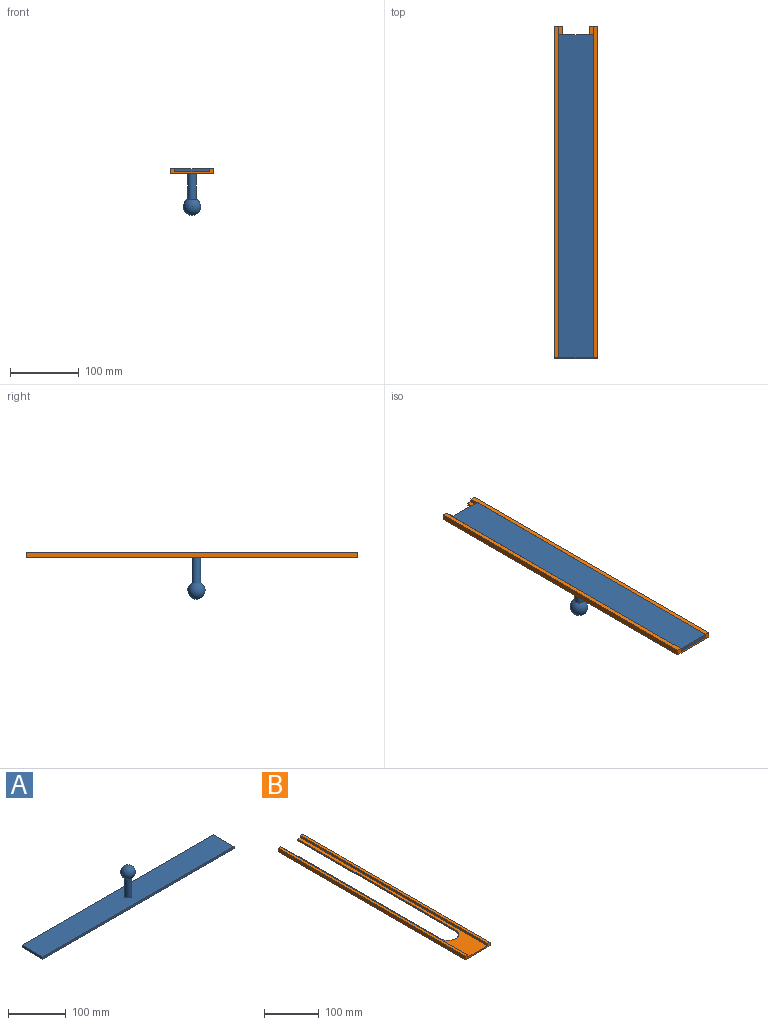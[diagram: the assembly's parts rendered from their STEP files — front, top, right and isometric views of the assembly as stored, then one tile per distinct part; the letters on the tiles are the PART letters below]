
ASSEMBLY  parts=2 mates=1
PART A: 8 faces, bbox 469.9x50.8x68.3 mm
  f0: cylinder r=6.35mm len=39.8mm, axis (0,0,-1), area 1588mm2, adj f5,f7
  f1: plane 50.8x4.76mm, normal (-1,0,0), area 241.9mm2, adj f2,f4,f5,f6
  f2: plane 469.9x4.76mm, normal (0,-1,0), area 2237.9mm2, adj f1,f3,f5,f6
  f3: plane 50.8x4.76mm, normal (1,0,0), area 241.9mm2, adj f2,f4,f5,f6
  f4: plane 469.9x4.76mm, normal (0,1,0), area 2237.9mm2, adj f1,f3,f5,f6
  f5: plane 469.9x50.8mm, normal (0,0,1), area 23744.2mm2, adj f0,f1,f2,f3,f4
  f6: plane 469.9x50.8mm, normal (0,0,-1), area 23870.9mm2, adj f1,f2,f3,f4
  f7: sphere r=12.7mm, area 1891.1mm2, adj f0
PART B: 14 faces, bbox 63.5x482.6x7.9 mm
  f0: plane 482.6x63.5mm, normal (0,0,-1), area 14591.2mm2, adj f2,f3,f8,f9,f10,f11,f12,f13
  f1: plane 482.6x50.8mm, normal (0,0,1), area 8462.2mm2, adj f2,f5,f6,f9,f10,f11,f12,f13
  f2: plane 12.7x7.94mm, normal (0,1,0), area 70.6mm2, adj f0,f1,f3,f4,f5,f11
  f3: plane 482.6x7.94mm, normal (1,0,0), area 3830.6mm2, adj f0,f2,f4,f9
  f4: plane 482.6x6.35mm, normal (0,0,1), area 3064.5mm2, adj f2,f3,f5,f9
  f5: plane 482.6x4.76mm, normal (-1,0,0), area 2298.4mm2, adj f1,f2,f4,f9
  f6: plane 482.6x4.76mm, normal (1,0,0), area 2298.4mm2, adj f1,f7,f9,f10
  f7: plane 482.6x6.35mm, normal (0,0,1), area 3064.5mm2, adj f6,f8,f9,f10
  f8: plane 482.6x7.94mm, normal (-1,0,0), area 3830.6mm2, adj f0,f7,f9,f10
  f9: plane 63.5x7.94mm, normal (0,-1,0), area 262.1mm2, adj f0,f1,f3,f4,f5,f6,f7,f8
  f10: plane 12.7x7.94mm, normal (0,1,0), area 70.6mm2, adj f0,f1,f6,f7,f8,f13
  f11: plane 406.4x3.18mm, normal (-1,0,0), area 1290.3mm2, adj f0,f1,f2,f12
  f12: cylinder r=19.05mm len=38.1mm, axis (0,0,-1), area 190mm2, adj f0,f1,f11,f13
  f13: plane 406.4x3.18mm, normal (1,0,0), area 1290.3mm2, adj f0,f1,f10,f12
PLACE A rot(axis=(-0.71,0.71,0),180deg) t=(25.4,-12.7,7.94)mm
PLACE B at identity fixed
MATE slider B.f9 <-> A.f3  axis (0,1,0) through (-25.4,-482.6,3.18)mm
